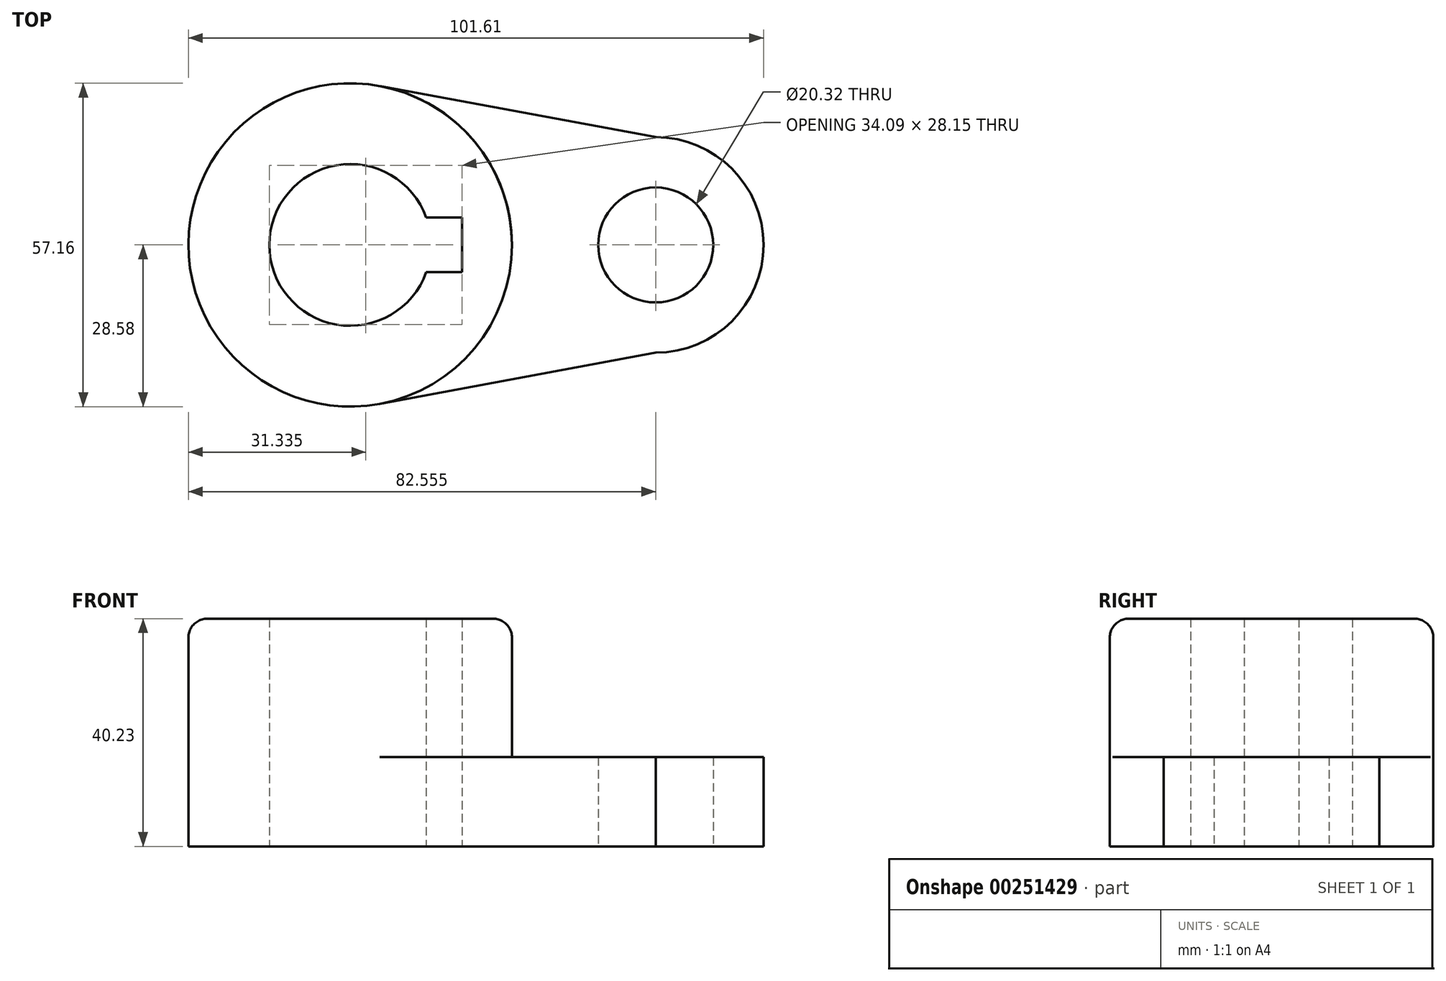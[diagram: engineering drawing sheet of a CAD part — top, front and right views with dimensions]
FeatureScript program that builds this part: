
annotation { "Feature Type Name" : "Feature", "Feature Type Description" : "" }
export const myFeature = defineFeature(function(context is Context, id is Id, definition is map)
    precondition{}
    {
        {
            var Q0;
            Q0=qCreatedBy(makeId("Top.planeOp"),FACE);
            var sketch = newSketch(context, id + "F0", { "sketchPlane" : qUnion([Q0])});
            skArc(sketch, "E0", {"start": v(13.45, 4.83) * mm, "mid": v(-14.29, 0) * mm, "end": v(13.45, -4.83) * mm});
            skCircle(sketch, "E1", {"center": v(53.98, 0) * mm, "radius": 10.16 * mm});
            skCircle(sketch, "E2", {"center": v(0, 0) * mm, "radius": 28.58 * mm});
            skCircle(sketch, "E3", {"center": v(53.98, 0) * mm, "radius": 19.05 * mm});
            skLineSegment(sketch, "E4.right", {"start": v(19.8, -4.83) * mm, "end": v(19.8, 4.83) * mm});
            skLineSegment(sketch, "E5.trimOffspring", {"start": v(13.45, 4.83) * mm, "end": v(19.8, 4.83) * mm});
            skLineSegment(sketch, "E6.trimOffspring", {"start": v(13.45, -4.83) * mm, "end": v(19.8, -4.83) * mm});
            skLineSegment(sketch, "E7", {"start": v(0, 0) * mm, "end": v(80.77, 0) * mm, "construction": true});
            skPoint(sketch, "E8.orphan", {"position": v(0, 28.58) * mm});
            skLineSegment(sketch, "E9", {"start": v(53.98, 19.05) * mm, "end": v(5.21, 28.1) * mm});
            skLineSegment(sketch, "E10", {"start": v(53.97, -19.05) * mm, "end": v(5.21, -28.1) * mm});
            skSolve(sketch);
        }
        {
            var Q0;
            Q0=makeQuery(id+"F0.imprint","IMPRINT",FACE,{"disambiguationData":[TD([[makeQuery(id+"F0.imprint","IMPRINT",EDGE,{"derivedFrom":sQuery(id+"F0.wireOp",EDGE,"E0")}),-1.0]])]});
            extrude(context, id + "F1", {"entities" : qUnion([Q0]), "depth" : 40.23 * mm});
        }
        {
            var Q0;
            {var subQ0=sQuery(id+"F0.wireOp",EDGE,"o5OdITKO-bEnJ-2VYi-a7Jk-zIUuU5JH3HSI");var subQ1=sQuery(id+"F0.wireOp",EDGE,"E2");var subQ2=makeQuery(id+"F0.imprint","INTERSECT",VERTEX,{"disambiguationData":[OD(1.0)],"derivedFrom":[subQ1,subQ0]});Q0=makeQuery(id+"F0.imprint","IMPRINT",FACE,{"disambiguationData":[TD([[makeQuery(id+"F0.imprint","IMPRINT",EDGE,{"disambiguationData":[TD([[subQ2,1.0]])],"derivedFrom":subQ1}),-1.0]])]});}
            var Q1;
            Q1=makeQuery(id+"F0.imprint","IMPRINT",FACE,{"disambiguationData":[TD([[makeQuery(id+"F0.imprint","IMPRINT",EDGE,{"derivedFrom":sQuery(id+"F0.wireOp",EDGE,"E1")}),-1.0]])]});
            extrude(context, id + "F2", {"entities" : qUnion([Q0, Q1]), "operationType" : NewBodyOperationType.ADD, "depth" : 15.77 * mm});
        }
        {
            var Q0;
            {var subQ0=sQuery(id+"F0.wireOp",EDGE,"E2");Q0=makeQuery(id+"F1.opExtrude","CAP_EDGE",EDGE,{"disambiguationData":[OSD([subQ0]),TDD([makeQuery(id+"F0.imprint","IMPRINT",EDGE,{"disambiguationData":[TD([[makeQuery(id+"F0.imprint","INTERSECT",VERTEX,{"disambiguationData":[OD(0.0)],"derivedFrom":[subQ0,sQuery(id+"F0.wireOp",EDGE,"SRnHb5uK-vhAm-8B8o-SrwD-EHZrL22LgCVp")]}),1.0]])],"derivedFrom":subQ0})])],"isStart":false});}
            var Q1;
            Q1=makeQuery(id+"F1.opExtrude","CAP_EDGE",EDGE,{"disambiguationData":[OSD([sQuery(id+"F0.wireOp",EDGE,"SRnHb5uK-vhAm-8B8o-SrwD-EHZrL22LgCVp")])],"isStart":false});
            var Q2;
            {var subQ0=sQuery(id+"F0.wireOp",EDGE,"E2");Q2=makeQuery(id+"F1.opExtrude","CAP_EDGE",EDGE,{"disambiguationData":[OSD([subQ0]),TDD([makeQuery(id+"F0.imprint","IMPRINT",EDGE,{"disambiguationData":[TD([[makeQuery(id+"F0.imprint","INTERSECT",VERTEX,{"disambiguationData":[OD(1.0)],"derivedFrom":[subQ0,sQuery(id+"F0.wireOp",EDGE,"o5OdITKO-bEnJ-2VYi-a7Jk-zIUuU5JH3HSI")]}),1.0]])],"derivedFrom":subQ0})])],"isStart":false});}
            var Q3;
            Q3=makeQuery(id+"F1.opExtrude","CAP_EDGE",EDGE,{"disambiguationData":[OSD([sQuery(id+"F0.wireOp",EDGE,"o5OdITKO-bEnJ-2VYi-a7Jk-zIUuU5JH3HSI")])],"isStart":false});
            fillet(context, id + "F3", {"entities" : qUnion([Q0, Q1, Q2, Q3]), "radius" : 3.3 * mm, "tangentPropagation" : true, "allowEdgeOverflow" : false});
        }
    });
